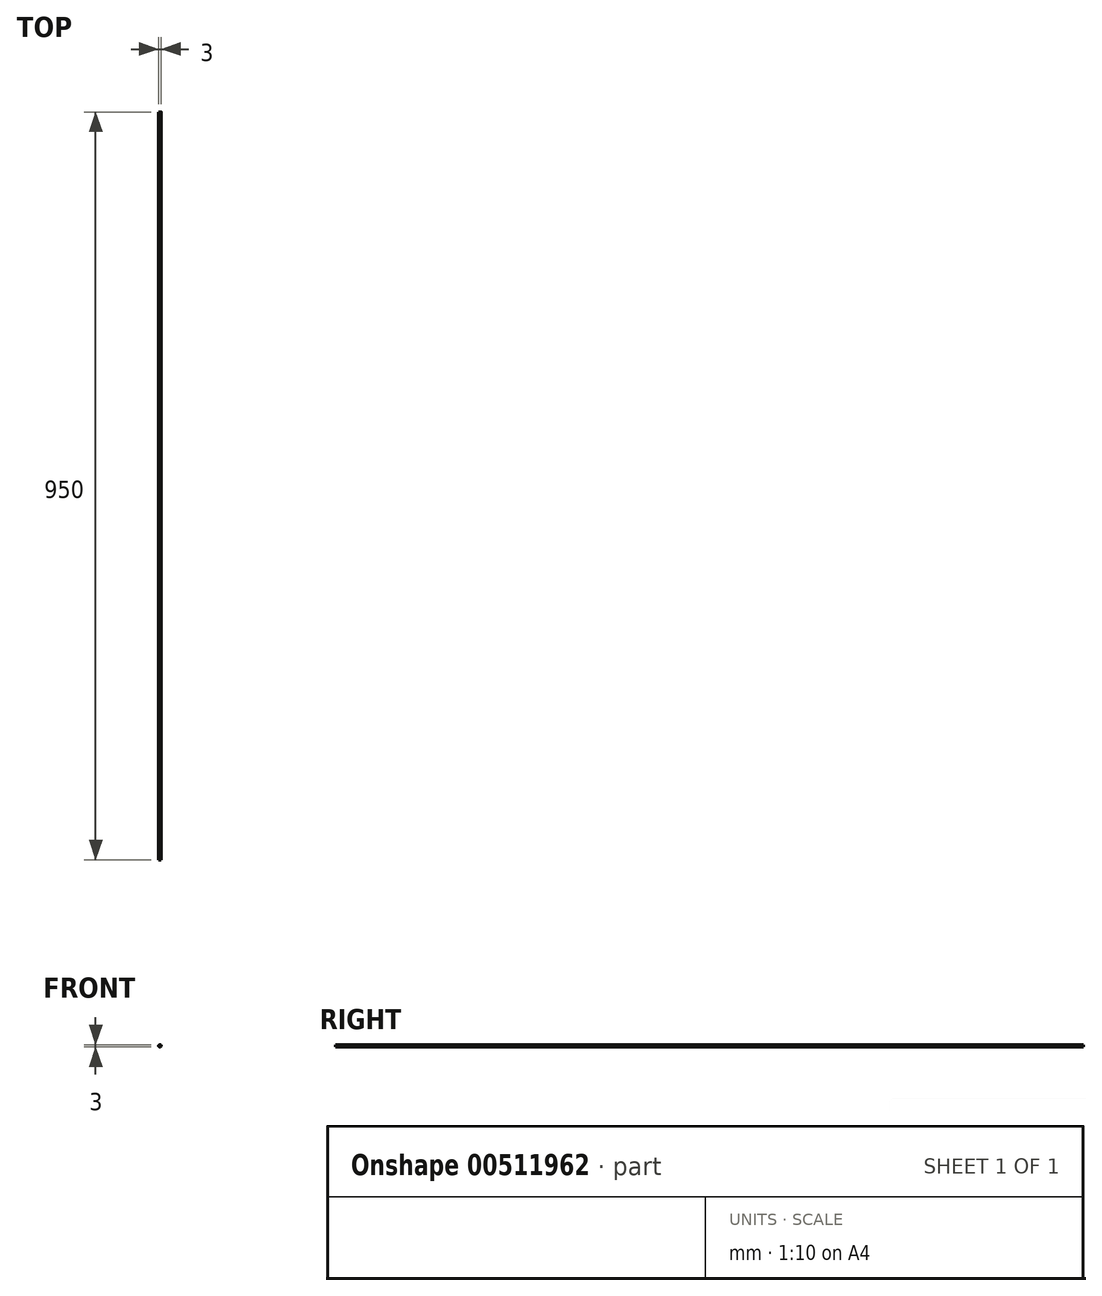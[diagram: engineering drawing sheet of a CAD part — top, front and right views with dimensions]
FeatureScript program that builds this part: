
annotation { "Feature Type Name" : "Feature", "Feature Type Description" : "" }
export const myFeature = defineFeature(function(context is Context, id is Id, definition is map)
    precondition{}
    {
        {
            var Q0;
            Q0=qCreatedBy(makeId("Front.planeOp"),FACE);
            var sketch = newSketch(context, id + "F0", { "sketchPlane" : qUnion([Q0])});
            skCircle(sketch, "E0", {"center": v(-4.29, 40.3) * mm, "radius": 1.5 * mm});
            skSolve(sketch);
        }
        {
            var Q0;
            Q0 = qSketchRegion(id + "F0", true);
            extrude(context, id + "F1", {"entities" : qUnion([Q0]), "depth" : 950 * mm, "offsetDistance" : 25 * mm});
        }
    });
